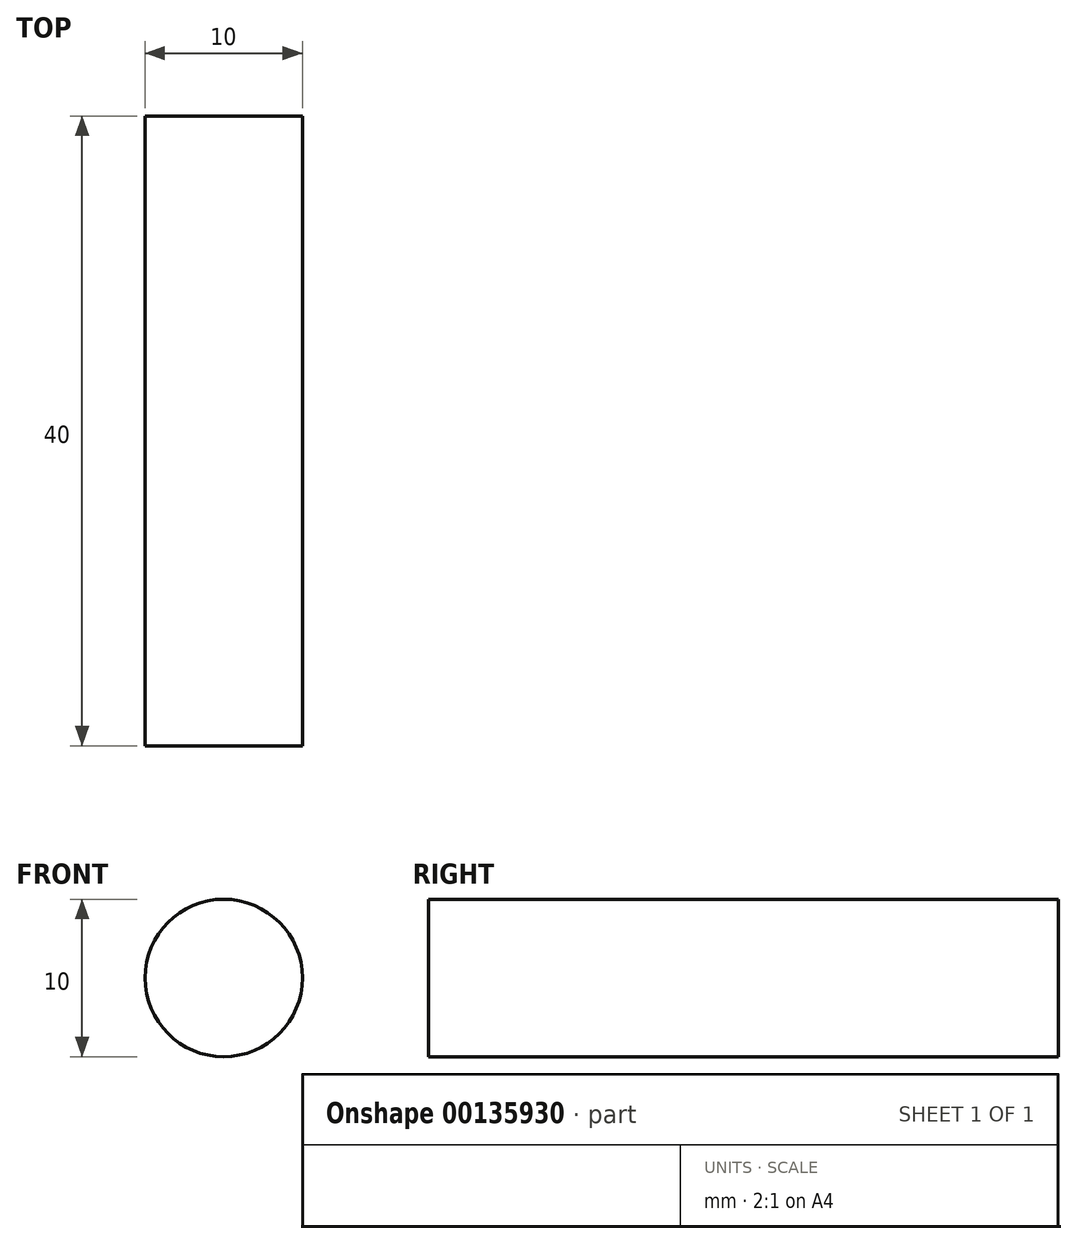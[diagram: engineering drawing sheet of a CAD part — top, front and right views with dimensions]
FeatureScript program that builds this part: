
annotation { "Feature Type Name" : "Feature", "Feature Type Description" : "" }
export const myFeature = defineFeature(function(context is Context, id is Id, definition is map)
    precondition{}
    {
        {
            var Q0;
            Q0=qCreatedBy(makeId("Front.planeOp"),FACE);
            var sketch = newSketch(context, id + "F0", { "sketchPlane" : qUnion([Q0])});
            skCircle(sketch, "E0", {"center": v(0, 0) * mm, "radius": 5 * mm});
            skLineSegment(sketch, "E1", {"start": v(0, 0) * mm, "end": v(5, 0) * mm});
            skSolve(sketch);
        }
        {
            var Q0;
            Q0=qSketchRegion(id+"F0",true);
            extrude(context, id + "F1", {"entities" : qUnion([Q0]), "depth" : 20 * mm, "hasSecondDirection" : true, "secondDirectionOppositeDirection" : true, "secondDirectionDepth" : 20 * mm});
        }
    });
